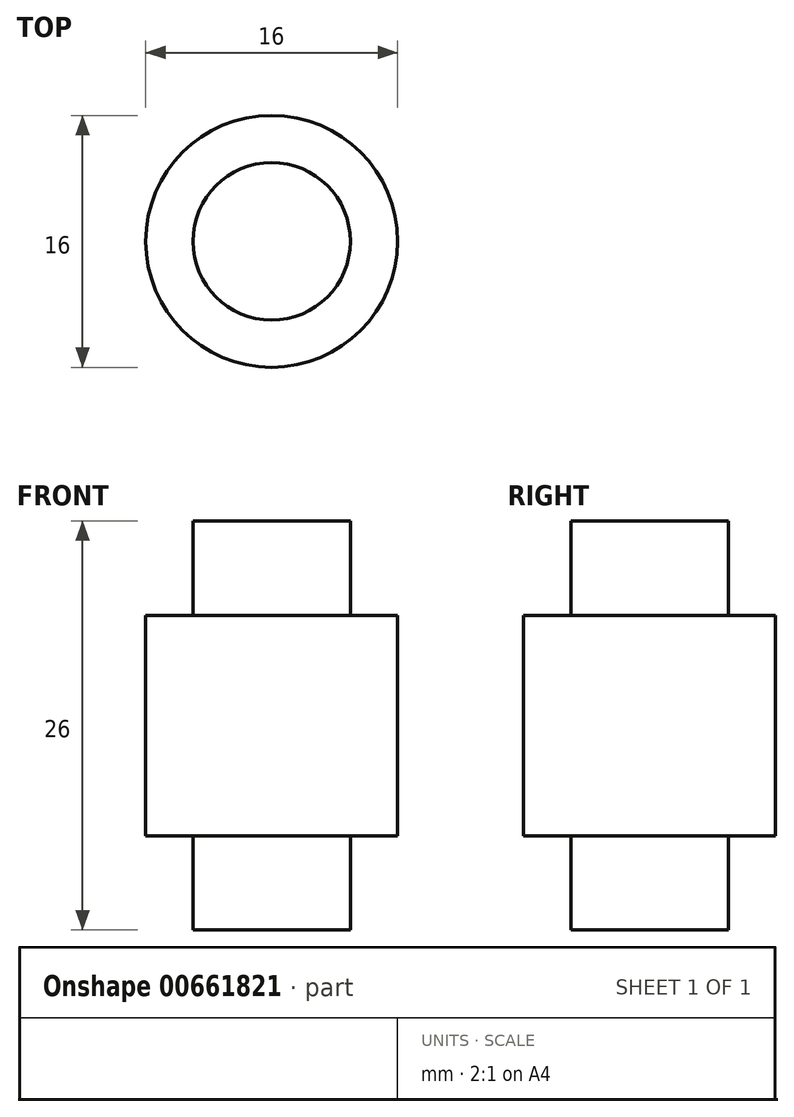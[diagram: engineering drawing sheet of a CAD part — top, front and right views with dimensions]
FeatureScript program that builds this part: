
annotation { "Feature Type Name" : "Feature", "Feature Type Description" : "" }
export const myFeature = defineFeature(function(context is Context, id is Id, definition is map)
    precondition{}
    {
        {
            var Q0;
            Q0=qCreatedBy(makeId("Top.planeOp"),FACE);
            var sketch = newSketch(context, id + "F0", { "sketchPlane" : qUnion([Q0])});
            skCircle(sketch, "E0", {"center": v(0, 0) * mm, "radius": 5 * mm});
            skSolve(sketch);
        }
        {
            var Q0;
            Q0 = qSketchRegion(id + "F0", true);
            extrude(context, id + "F1", {"entities" : qUnion([Q0]), "depth" : 6 * mm, "offsetDistance" : 25 * mm});
        }
        {
            var Q0;
            Q0=makeQuery(id+"F1.opExtrude","CAP_FACE",FACE,{"disambiguationData":[OSD([sQuery(id+"F0.wireOp",EDGE,"E0")])],"isStart":false});
            var sketch = newSketch(context, id + "F2", { "sketchPlane" : qUnion([Q0])});
            skCircle(sketch, "E1", {"center": v(0, 0) * mm, "radius": 8 * mm});
            skSolve(sketch);
        }
        {
            var Q0;
            Q0=makeQuery(id+"F2.imprint","IMPRINT",FACE,{"disambiguationData":[TD([[makeQuery(id+"F2.imprint","IMPRINT",EDGE,{"derivedFrom":sQuery(id+"F2.wireOp",EDGE,"E1")}),1.0]])]});
            var Q1;
            Q1=makeQuery(id+"F2.imprint","IMPRINT",FACE,{"disambiguationData":[TD([[makeQuery(id+"F2.imprint","IMPRINT",EDGE,{"derivedFrom":makeQuery(id+"F1.opExtrude","CAP_EDGE",EDGE,{"disambiguationData":[OSD([sQuery(id+"F0.wireOp",EDGE,"E0")])],"isStart":false})}),1.0]])]});
            var Q2;
            Q2=sQuery(id+"F2.wireOp",EDGE,"E1");
            extrude(context, id + "F3", {"entities" : qUnion([Q0, Q1]), "operationType" : NewBodyOperationType.ADD, "surfaceEntities" : qUnion([Q2]), "depth" : 14 * mm, "offsetDistance" : 25 * mm});
        }
        {
            var Q0;
            Q0=makeQuery(id+"F3.opExtrude","CAP_FACE",FACE,{"disambiguationData":[OSD([sQuery(id+"F2.wireOp",EDGE,"E1")])],"isStart":false});
            var sketch = newSketch(context, id + "F4", { "sketchPlane" : qUnion([Q0])});
            skCircle(sketch, "E2", {"center": v(0, 0) * mm, "radius": 5 * mm});
            skSolve(sketch);
        }
        {
            var Q0;
            Q0 = qSketchRegion(id + "F4", true);
            extrude(context, id + "F5", {"entities" : qUnion([Q0]), "operationType" : NewBodyOperationType.ADD, "depth" : 6 * mm, "offsetDistance" : 25 * mm});
        }
    });
